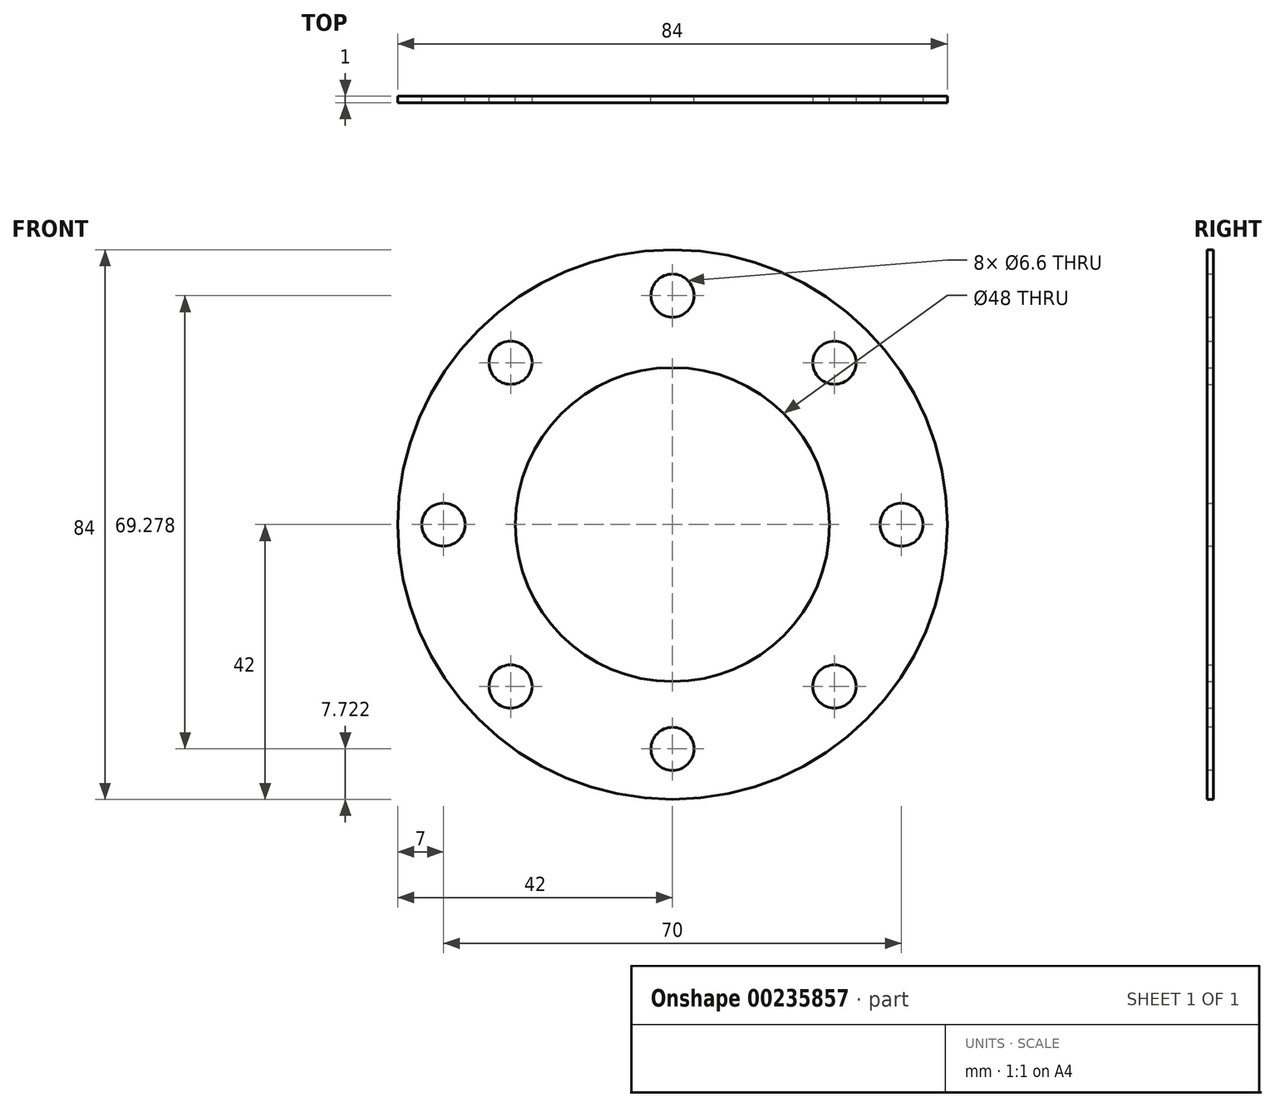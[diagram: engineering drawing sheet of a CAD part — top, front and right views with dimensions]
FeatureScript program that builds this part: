
annotation { "Feature Type Name" : "Feature", "Feature Type Description" : "" }
export const myFeature = defineFeature(function(context is Context, id is Id, definition is map)
    precondition{}
    {
        {
            var Q0;
            Q0=qCreatedBy(makeId("Front.planeOp"),FACE);
            var sketch = newSketch(context, id + "F0", { "sketchPlane" : qUnion([Q0])});
            skCircle(sketch, "E0", {"center": v(0, 0) * mm, "radius": 42 * mm});
            skCircle(sketch, "E1", {"center": v(0, 0) * mm, "radius": 35 * mm, "construction": true});
            skCircle(sketch, "E2", {"center": v(0, 0) * mm, "radius": 24 * mm});
            skLineSegment(sketch, "E3", {"start": v(0, 0) * mm, "end": v(75.61, 0) * mm, "construction": true});
            skLineSegment(sketch, "E4", {"start": v(0, 0) * mm, "end": v(0, 70.56) * mm, "construction": true});
            skLineSegment(sketch, "E5", {"start": v(0, 0) * mm, "end": v(62.47, 62.47) * mm, "construction": true});
            skCircle(sketch, "E6", {"center": v(0, 35) * mm, "radius": 3.3 * mm});
            skPoint(sketch, "E6.centerSnap0", {"position": v(0, 35.28) * mm});
            skCircle(sketch, "E7", {"center": v(35, 0) * mm, "radius": 3.3 * mm});
            skCircle(sketch, "E8", {"center": v(24.75, 24.75) * mm, "radius": 3.3 * mm});
            skLineSegment(sketch, "E9", {"start": v(0, 0) * mm, "end": v(0, -68.56) * mm, "construction": true});
            skLineSegment(sketch, "E10", {"start": v(0, 0) * mm, "end": v(54.56, -54.56) * mm, "construction": true});
            skCircle(sketch, "E11", {"center": v(24.75, -24.75) * mm, "radius": 3.3 * mm});
            skCircle(sketch, "E12", {"center": v(0, -34.28) * mm, "radius": 3.3 * mm});
            skCircle(sketch, "E13.MirrorC", {"center": v(-24.75, 24.75) * mm, "radius": 3.3 * mm});
            skCircle(sketch, "E14.MirrorC", {"center": v(-35, 0) * mm, "radius": 3.3 * mm});
            skCircle(sketch, "E15.MirrorC", {"center": v(-24.75, -24.75) * mm, "radius": 3.3 * mm});
            skSolve(sketch);
        }
        {
            var Q0;
            Q0=makeQuery(id+"F0.imprint","IMPRINT",FACE,{"disambiguationData":[TD([[makeQuery(id+"F0.imprint","IMPRINT",EDGE,{"derivedFrom":sQuery(id+"F0.wireOp",EDGE,"E0")}),1.0]])]});
            var Q1;
            Q1=makeQuery(id+"F0.imprint","IMPRINT",FACE,{"disambiguationData":[TD([[makeQuery(id+"F0.imprint","IMPRINT",EDGE,{"derivedFrom":sQuery(id+"F0.wireOp",EDGE,"E6")}),-1.0]])]});
            var Q2;
            Q2=makeQuery(id+"F0.imprint","IMPRINT",FACE,{"disambiguationData":[TD([[makeQuery(id+"F0.imprint","IMPRINT",EDGE,{"derivedFrom":sQuery(id+"F0.wireOp",EDGE,"E13.MirrorC")}),-1.0]])]});
            var Q3;
            Q3=makeQuery(id+"F0.imprint","IMPRINT",FACE,{"disambiguationData":[TD([[makeQuery(id+"F0.imprint","IMPRINT",EDGE,{"derivedFrom":sQuery(id+"F0.wireOp",EDGE,"E15.MirrorC")}),-1.0]])]});
            var Q4;
            Q4=makeQuery(id+"F0.imprint","IMPRINT",FACE,{"disambiguationData":[TD([[makeQuery(id+"F0.imprint","IMPRINT",EDGE,{"derivedFrom":sQuery(id+"F0.wireOp",EDGE,"E14.MirrorC")}),-1.0]])]});
            var Q5;
            Q5=makeQuery(id+"F0.imprint","IMPRINT",FACE,{"disambiguationData":[TD([[makeQuery(id+"F0.imprint","IMPRINT",EDGE,{"derivedFrom":sQuery(id+"F0.wireOp",EDGE,"E12")}),1.0]])]});
            var Q6;
            Q6=makeQuery(id+"F0.imprint","IMPRINT",FACE,{"disambiguationData":[TD([[makeQuery(id+"F0.imprint","IMPRINT",EDGE,{"derivedFrom":sQuery(id+"F0.wireOp",EDGE,"E11")}),1.0]])]});
            var Q7;
            Q7=makeQuery(id+"F0.imprint","IMPRINT",FACE,{"disambiguationData":[TD([[makeQuery(id+"F0.imprint","IMPRINT",EDGE,{"derivedFrom":sQuery(id+"F0.wireOp",EDGE,"E7")}),1.0]])]});
            var Q8;
            Q8=makeQuery(id+"F0.imprint","IMPRINT",FACE,{"disambiguationData":[TD([[makeQuery(id+"F0.imprint","IMPRINT",EDGE,{"derivedFrom":sQuery(id+"F0.wireOp",EDGE,"E8")}),1.0]])]});
            extrude(context, id + "F1", {"entities" : qUnion([Q0, Q1, Q2, Q3, Q4, Q5, Q6, Q7, Q8]), "depth" : 1 * mm});
        }
        {
            var Q0;
            Q0=sQuery(id+"F0.wireOp",VERTEX,"E8.center");
            var Q1;
            Q1=sQuery(id+"F0.wireOp",VERTEX,"E7.center");
            var Q2;
            Q2=sQuery(id+"F0.wireOp",VERTEX,"E11.center");
            var Q3;
            Q3=sQuery(id+"F0.wireOp",VERTEX,"E12.center");
            var Q4;
            Q4=sQuery(id+"F0.wireOp",VERTEX,"E15.MirrorC.center");
            var Q5;
            Q5=sQuery(id+"F0.wireOp",VERTEX,"E14.MirrorC.center");
            var Q6;
            Q6=sQuery(id+"F0.wireOp",VERTEX,"E13.MirrorC.center");
            var Q7;
            Q7=sQuery(id+"F0.wireOp",VERTEX,"E6.center");
            var Q8;
            Q8=makeQuery(id+"F1.opExtrude","SWEPT_BODY",BODY,{"disambiguationData":[OSD([sQuery(id+"F0.wireOp",EDGE,"E0"),sQuery(id+"F0.wireOp",EDGE,"E2")])]});
            hole(context, id + "F2", {"style" : HoleStyle.SIMPLE, "endStyle" : HoleEndStyle.THROUGH, "oppositeDirection" : true, "standardTappedOrClearance" : lookupTablePath({ "standard" : "ISO", "fit" : "Normal", "size" : "M6", "type" : "Clearance" }), "standardBlindInLast" : lookupTablePath({ "fit" : "Standard", "standard" : "ISO", "size" : "M6", "type" : "Clearance" }), "holeDiameter" : 6.6 * mm, "tappedDepth" : 7.9 * mm, "tapClearance" : 3, "startFromSketch" : true, "locations" : qUnion([Q0, Q1, Q2, Q3, Q4, Q5, Q6, Q7]), "scope" : qUnion([Q8])});
        }
    });
